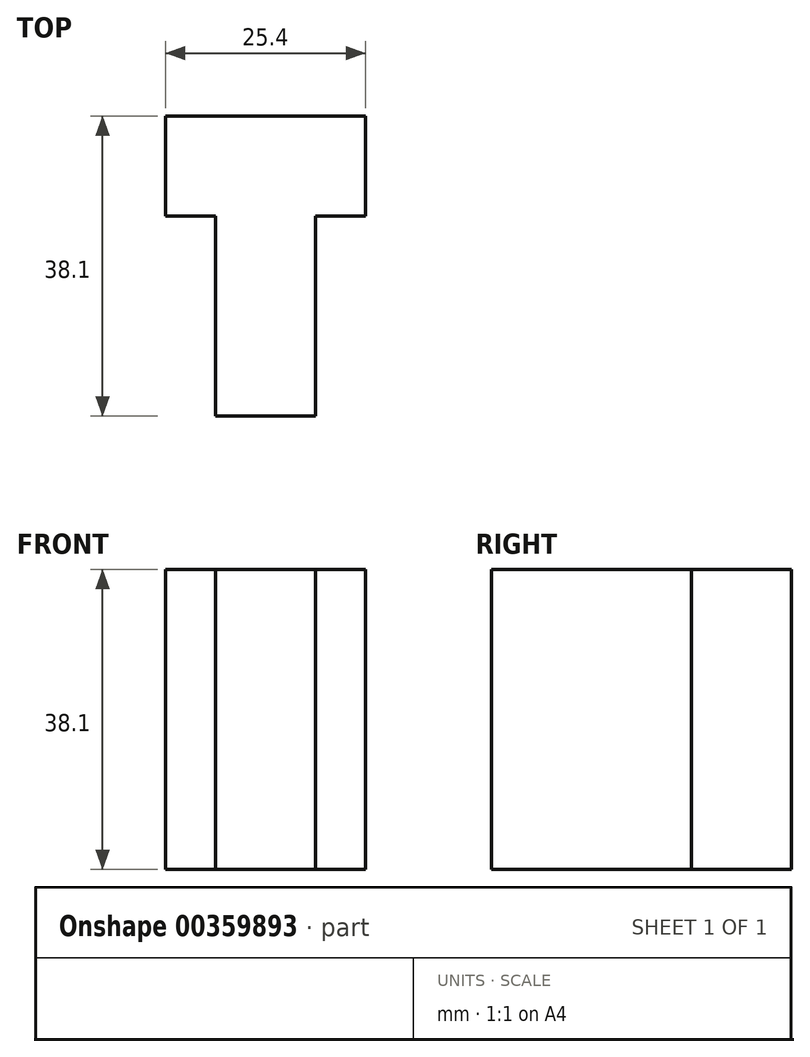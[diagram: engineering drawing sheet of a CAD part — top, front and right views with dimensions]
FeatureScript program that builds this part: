
annotation { "Feature Type Name" : "Feature", "Feature Type Description" : "" }
export const myFeature = defineFeature(function(context is Context, id is Id, definition is map)
    precondition{}
    {
        {
            var Q0;
            Q0=qCreatedBy(makeId("Top.planeOp"),FACE);
            var sketch = newSketch(context, id + "F0", { "sketchPlane" : qUnion([Q0])});
            skLineSegment(sketch, "E0", {"start": v(12.7, 0) * mm, "end": v(12.7, 25.4) * mm});
            skLineSegment(sketch, "E1", {"start": v(12.7, 25.4) * mm, "end": v(19.05, 25.4) * mm});
            skLineSegment(sketch, "E2", {"start": v(19.05, 25.4) * mm, "end": v(19.05, 38.1) * mm});
            skLineSegment(sketch, "E3", {"start": v(19.05, 38.1) * mm, "end": v(-6.35, 38.1) * mm});
            skLineSegment(sketch, "E4", {"start": v(-6.35, 38.1) * mm, "end": v(-6.35, 25.4) * mm});
            skLineSegment(sketch, "E5", {"start": v(-6.35, 25.4) * mm, "end": v(0, 25.4) * mm});
            skLineSegment(sketch, "E6", {"start": v(0, 25.4) * mm, "end": v(0, 0) * mm});
            skLineSegment(sketch, "E7", {"start": v(0, 0) * mm, "end": v(12.7, 0) * mm});
            skSolve(sketch);
        }
        {
            var Q0;
            Q0 = qSketchRegion(id + "F0", true);
            extrude(context, id + "F1", {"entities" : qUnion([Q0]), "depth" : 38.1 * mm});
        }
    });
